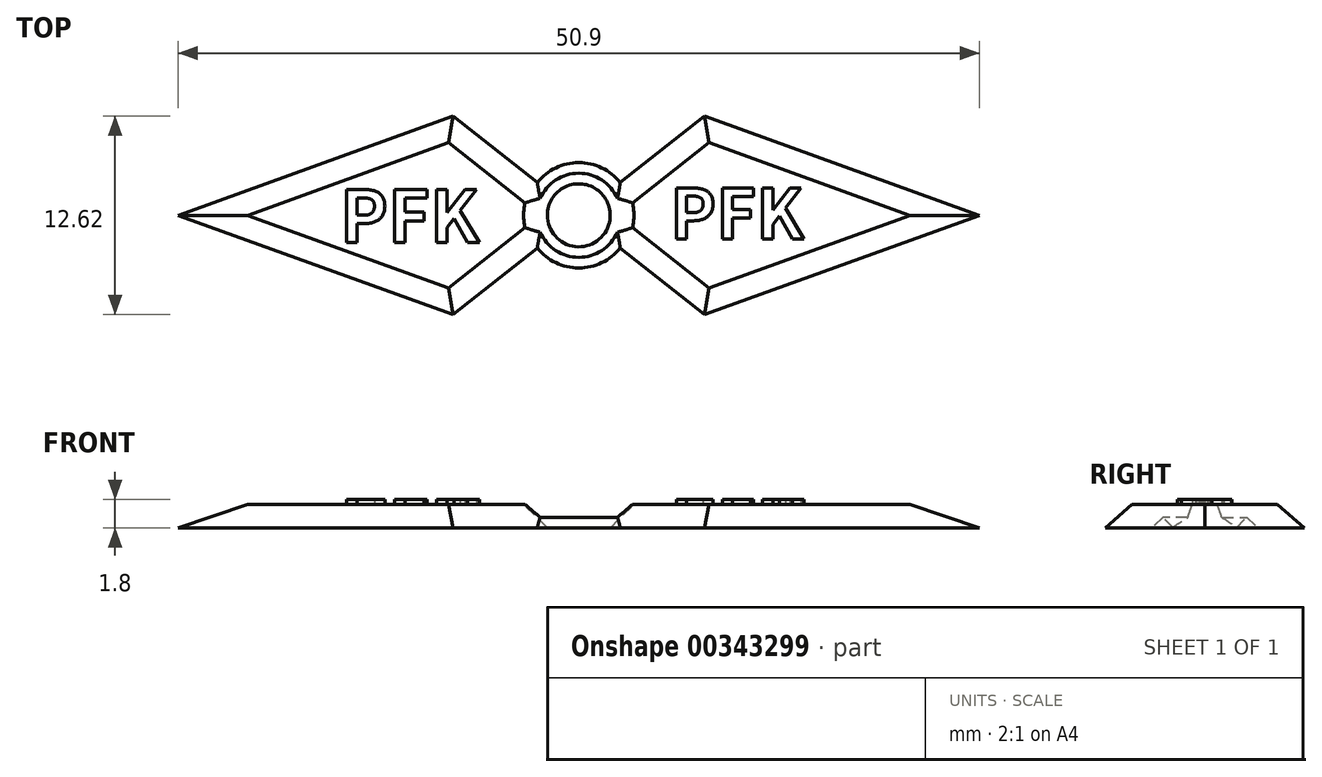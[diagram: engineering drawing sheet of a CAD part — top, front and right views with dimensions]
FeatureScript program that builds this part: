
annotation { "Feature Type Name" : "Feature", "Feature Type Description" : "" }
export const myFeature = defineFeature(function(context is Context, id is Id, definition is map)
    precondition{}
    {
        {
            var Q0;
            Q0=qCreatedBy(makeId("Top.planeOp"),FACE);
            var sketch = newSketch(context, id + "F0", { "sketchPlane" : qUnion([Q0])});
            skCircle(sketch, "E0", {"center": v(0, 0) * mm, "radius": 3.35 * mm});
            skLineSegment(sketch, "E1", {"start": v(0, 0) * mm, "end": v(7.99, -6.31) * mm});
            skLineSegment(sketch, "E2", {"start": v(7.99, -6.31) * mm, "end": v(25.45, 0) * mm});
            skLineSegment(sketch, "E3.MirrorCS", {"start": v(7.99, 6.31) * mm, "end": v(25.45, 0) * mm});
            skLineSegment(sketch, "E4.MirrorCS", {"start": v(0, 0) * mm, "end": v(7.99, 6.31) * mm});
            skLineSegment(sketch, "E5.MirrorCS", {"start": v(0, 0) * mm, "end": v(-7.99, 6.31) * mm});
            skLineSegment(sketch, "E6.MirrorCS", {"start": v(0, 0) * mm, "end": v(-7.99, -6.31) * mm});
            skLineSegment(sketch, "E7.MirrorCS", {"start": v(-7.99, -6.31) * mm, "end": v(-25.45, 0) * mm});
            skLineSegment(sketch, "E8.MirrorCS", {"start": v(-7.99, 6.31) * mm, "end": v(-25.45, 0) * mm});
            skSolve(sketch);
        }
        {
            var Q0;
            Q0 = qSketchRegion(id + "F0", true);
            extrude(context, id + "F1", {"entities" : qUnion([Q0]), "depth" : 1.5 * mm});
        }
        {
            var Q0;
            Q0=qCreatedBy(makeId("Top.planeOp"),FACE);
            var sketch = newSketch(context, id + "F2", { "sketchPlane" : qUnion([Q0])});
            skCircle(sketch, "E9", {"center": v(0, 0) * mm, "radius": 1.97 * mm});
            skSolve(sketch);
        }
        {
            var Q0;
            Q0=sQuery(id+"F2.wireOp",VERTEX,"E9.center");
            var Q1;
            Q1=makeQuery(id+"F1.opExtrude","SWEPT_BODY",BODY,{"disambiguationData":[OSD([sQuery(id+"F0.wireOp",EDGE,"E0"),sQuery(id+"F0.wireOp",EDGE,"E1"),sQuery(id+"F0.wireOp",EDGE,"E2"),sQuery(id+"F0.wireOp",EDGE,"E3.MirrorCS"),sQuery(id+"F0.wireOp",EDGE,"E4.MirrorCS"),sQuery(id+"F0.wireOp",EDGE,"E5.MirrorCS"),sQuery(id+"F0.wireOp",EDGE,"E6.MirrorCS"),sQuery(id+"F0.wireOp",EDGE,"E7.MirrorCS"),sQuery(id+"F0.wireOp",EDGE,"E8.MirrorCS")])]});
            hole(context, id + "F3", {"style" : HoleStyle.SIMPLE, "endStyle" : HoleEndStyle.THROUGH, "oppositeDirection" : true, "holeDiameter" : 4 * mm, "isTappedThrough" : true, "tappedDepth" : 12 * mm, "tapClearance" : 3, "locations" : qUnion([Q0]), "scope" : qUnion([Q1])});
        }
        {
            var Q0;
            Q0=makeQuery(id+"F1.opExtrude","CAP_FACE",FACE,{"disambiguationData":[OSD([sQuery(id+"F0.wireOp",EDGE,"E0"),sQuery(id+"F0.wireOp",EDGE,"E1"),sQuery(id+"F0.wireOp",EDGE,"E2"),sQuery(id+"F0.wireOp",EDGE,"E3.MirrorCS"),sQuery(id+"F0.wireOp",EDGE,"E4.MirrorCS"),sQuery(id+"F0.wireOp",EDGE,"E5.MirrorCS"),sQuery(id+"F0.wireOp",EDGE,"E6.MirrorCS"),sQuery(id+"F0.wireOp",EDGE,"E7.MirrorCS"),sQuery(id+"F0.wireOp",EDGE,"E8.MirrorCS")])],"isStart":false});
            chamfer(context, id + "F4", {"entities" : qUnion([Q0]), "width" : 1.5 * mm, "tangentPropagation" : true});
        }
        {
            var Q0;
            Q0=qCreatedBy(makeId("Top.planeOp"),FACE);
            var sketch = newSketch(context, id + "F5", { "sketchPlane" : qUnion([Q0])});
            skText(sketch, "E10", { "text": "PFK", "fontName": "NotoSansCJKkr-Bold.otf"});
            skText(sketch, "E11", { "text": "PFK", "fontName": "NotoSansCJKkr-Bold.otf"});
            const initialGuessF5  = {"E10": [-0.01516, -0.00173, 1, 0, 0.00328], "E11": [0.0058, -0.0015, 1, 0, 0.00315]};
            skSetInitialGuess(sketch, initialGuessF5);
            skSolve(sketch);
        }
        {
            var Q0;
            Q0 = qSketchRegion(id + "F5", true);
            extrude(context, id + "F6", {"entities" : qUnion([Q0]), "operationType" : NewBodyOperationType.ADD, "depth" : 1.8 * mm});
        }
    });
